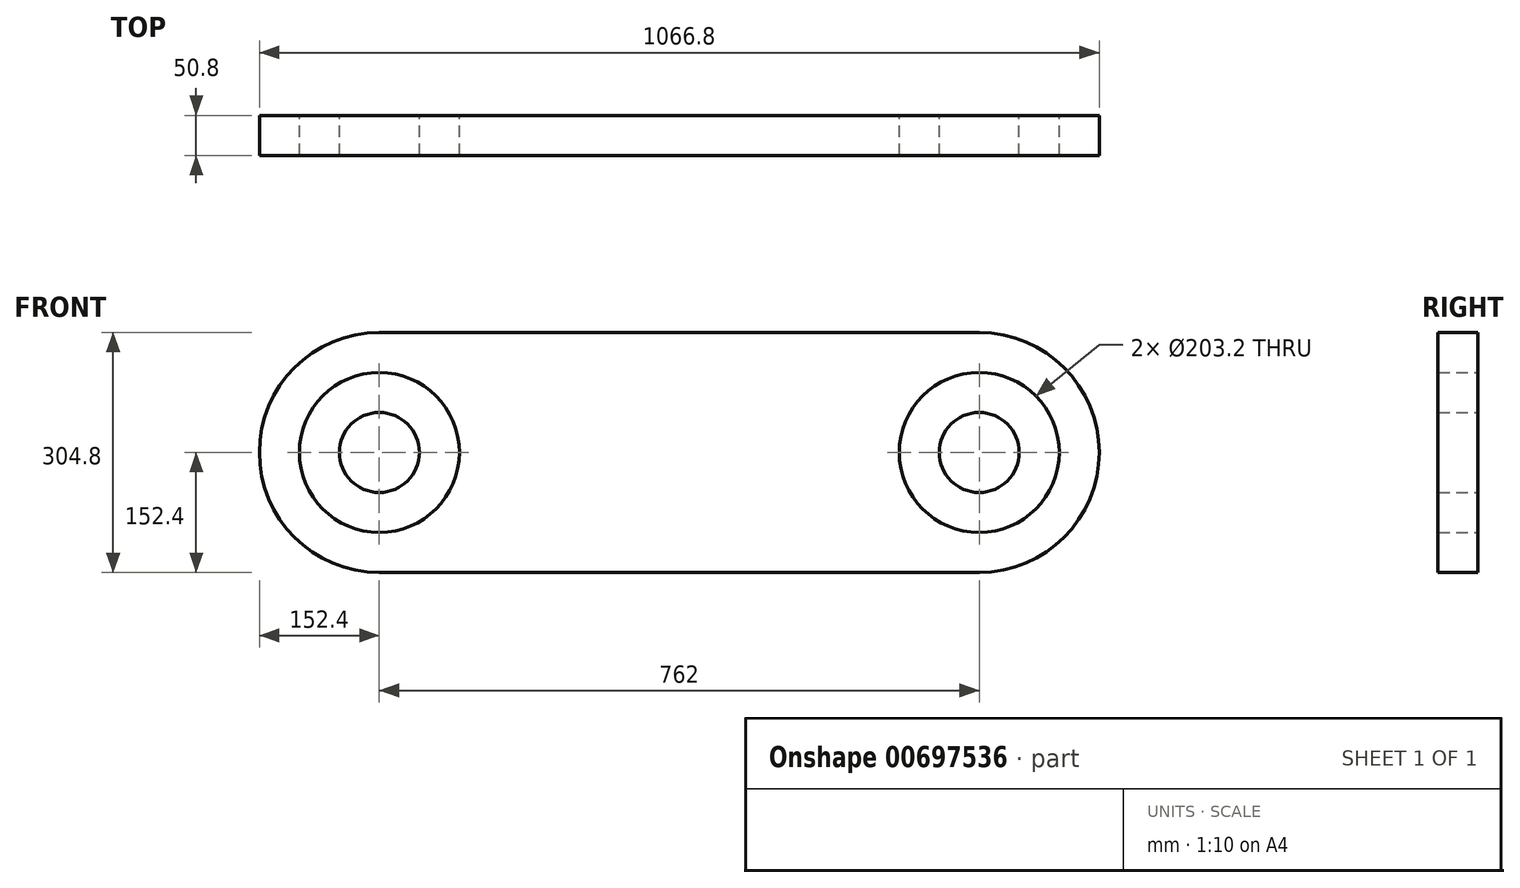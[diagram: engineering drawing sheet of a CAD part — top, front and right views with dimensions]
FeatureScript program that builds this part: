
annotation { "Feature Type Name" : "Feature", "Feature Type Description" : "" }
export const myFeature = defineFeature(function(context is Context, id is Id, definition is map)
    precondition{}
    {
        {
            var Q0;
            Q0=qCreatedBy(makeId("Front.planeOp"),FACE);
            var sketch = newSketch(context, id + "F0", { "sketchPlane" : qUnion([Q0])});
            skCircle(sketch, "E0", {"center": v(-381, 0) * mm, "radius": 101.6 * mm});
            skCircle(sketch, "E1", {"center": v(-381, 0) * mm, "radius": 50.8 * mm});
            skCircle(sketch, "E2", {"center": v(-381, 0) * mm, "radius": 152.4 * mm});
            skLineSegment(sketch, "E3", {"start": v(-381, 152.4) * mm, "end": v(0, 152.4) * mm});
            skLineSegment(sketch, "E4", {"start": v(0, 152.4) * mm, "end": v(0, -152.4) * mm});
            skLineSegment(sketch, "E5", {"start": v(0, -152.4) * mm, "end": v(-381, -152.4) * mm});
            skSolve(sketch);
        }
        {
            var Q0;
            Q0=makeQuery(id+"F0.imprint","IMPRINT",FACE,{"disambiguationData":[TD([[makeQuery(id+"F0.imprint","IMPRINT",EDGE,{"derivedFrom":sQuery(id+"F0.wireOp",EDGE,"E1")}),1.0]])]});
            var Q1;
            Q1=makeQuery(id+"F0.imprint","IMPRINT",FACE,{"disambiguationData":[TD([[makeQuery(id+"F0.imprint","IMPRINT",EDGE,{"derivedFrom":sQuery(id+"F0.wireOp",EDGE,"E0")}),-1.0]])]});
            var Q2;
            {var subQ0=sQuery(id+"F0.wireOp",EDGE,"E3");Q2=makeQuery(id+"F0.imprint","IMPRINT",FACE,{"disambiguationData":[TD([[makeQuery(id+"F0.imprint","IMPRINT",EDGE,{"derivedFrom":subQ0}),-1.0]])]});}
            extrude(context, id + "F1", {"entities" : qUnion([Q0, Q1, Q2]), "depth" : 50.8 * mm, "offsetDistance" : 25.4 * mm});
        }
        {
            var Q0;
            Q0=makeQuery(id+"F1.opExtrude","SWEPT_BODY",BODY,{"disambiguationData":[OSD([sQuery(id+"F0.wireOp",EDGE,"E0"),sQuery(id+"F0.wireOp",EDGE,"E2"),sQuery(id+"F0.wireOp",EDGE,"E3"),sQuery(id+"F0.wireOp",EDGE,"E4"),sQuery(id+"F0.wireOp",EDGE,"E5")])]});
            var Q1;
            Q1=makeQuery(id+"F1.opExtrude","SWEPT_BODY",BODY,{"disambiguationData":[OSD([sQuery(id+"F0.wireOp",EDGE,"E1")])]});
            var Q2;
            Q2=makeQuery(id+"F1.opExtrude","SWEPT_FACE",FACE,{"disambiguationData":[OSD([sQuery(id+"F0.wireOp",EDGE,"E4")])]});
            mirror(context, id + "F2", {"operationType" : NewBodyOperationType.ADD, "entities" : qUnion([Q0, Q1]), "mirrorPlane" : qUnion([Q2])});
        }
    });
